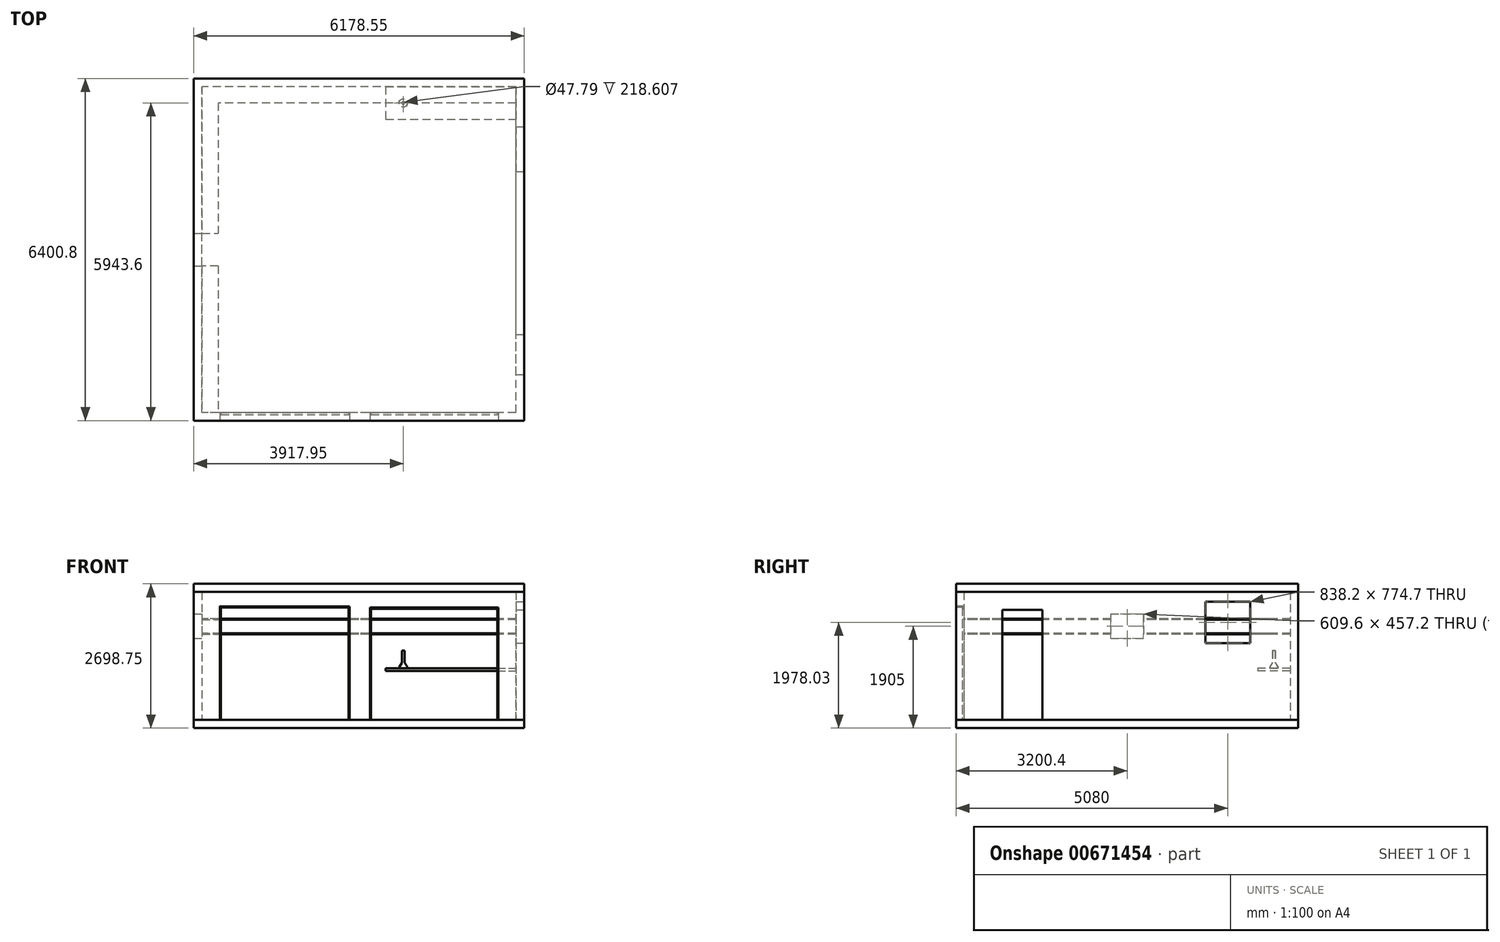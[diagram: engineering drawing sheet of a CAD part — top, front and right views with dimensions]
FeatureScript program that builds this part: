
annotation { "Feature Type Name" : "Feature", "Feature Type Description" : "" }
export const myFeature = defineFeature(function(context is Context, id is Id, definition is map)
    precondition{}
    {
        {
            var Q0;
            Q0=qCreatedBy(makeId("Top.planeOp"),FACE);
            var sketch = newSketch(context, id + "F0", { "sketchPlane" : qUnion([Q0])});
            skLineSegment(sketch, "E0.bottom", {"start": v(0, 0) * mm, "end": v(-5873.75, 0) * mm});
            skLineSegment(sketch, "E0.top", {"start": v(0, 6096) * mm, "end": v(-5873.75, 6096) * mm});
            skLineSegment(sketch, "E0.left", {"start": v(0, 0) * mm, "end": v(0, 6096) * mm});
            skLineSegment(sketch, "E0.right", {"start": v(-5873.75, 0) * mm, "end": v(-5873.75, 6096) * mm});
            skLineSegment(sketch, "E1.0", {"start": v(152.4, 6248.4) * mm, "end": v(-6026.15, 6248.4) * mm});
            skLineSegment(sketch, "E1.1", {"start": v(152.4, -152.4) * mm, "end": v(152.4, 6248.4) * mm});
            skLineSegment(sketch, "E1.2", {"start": v(152.4, -152.4) * mm, "end": v(-6026.15, -152.4) * mm});
            skLineSegment(sketch, "E1.3", {"start": v(-6026.15, -152.4) * mm, "end": v(-6026.15, 6248.4) * mm});
            skSolve(sketch);
        }
        {
            var Q0;
            Q0 = qSketchRegion(id + "F0", true);
            extrude(context, id + "F1", {"entities" : qUnion([Q0]), "depth" : 2393.95 * mm, "offsetDistance" : 25.4 * mm});
        }
        {
            var Q0;
            Q0=makeQuery(id+"F1.opExtrude","SWEPT_FACE",FACE,{"disambiguationData":[OSD([sQuery(id+"F0.wireOp",EDGE,"E1.1")])]});
            var sketch = newSketch(context, id + "F2", { "sketchPlane" : qUnion([Q0])});
            skLineSegment(sketch, "E2.bottom", {"start": v(711.2, 0) * mm, "end": v(1460.5, 0) * mm});
            skLineSegment(sketch, "E2.top", {"start": v(711.2, 2057.4) * mm, "end": v(1460.5, 2057.4) * mm});
            skLineSegment(sketch, "E2.left", {"start": v(711.2, 0) * mm, "end": v(711.2, 2057.4) * mm});
            skLineSegment(sketch, "E2.right", {"start": v(1460.5, 0) * mm, "end": v(1460.5, 2057.4) * mm});
            skSolve(sketch);
        }
        {
            var Q0;
            Q0=makeQuery(id+"F2.imprint","IMPRINT",FACE,{"disambiguationData":[TD([[makeQuery(id+"F2.imprint","IMPRINT",EDGE,{"derivedFrom":sQuery(id+"F2.wireOp",EDGE,"E2.bottom")}),1.0]])]});
            var Q1;
            Q1=makeQuery(id+"F1.opExtrude","SWEPT_FACE",FACE,{"disambiguationData":[OSD([sQuery(id+"F0.wireOp",EDGE,"E0.left")])]});
            extrude(context, id + "F3", {"entities" : qUnion([Q0]), "operationType" : NewBodyOperationType.REMOVE, "endBound" : BoundingType.UP_TO_SURFACE, "oppositeDirection" : true, "depth" : 25.4 * mm, "endBoundEntityFace" : qUnion([Q1]), "offsetDistance" : 25.4 * mm});
        }
        {
            var Q0;
            Q0=makeQuery(id+"F1.opExtrude","SWEPT_FACE",FACE,{"disambiguationData":[OSD([sQuery(id+"F0.wireOp",EDGE,"E1.2")])]});
            var sketch = newSketch(context, id + "F4", { "sketchPlane" : qUnion([Q0])});
            skLineSegment(sketch, "E3.bottom", {"start": v(-5537.2, 0) * mm, "end": v(-3111.5, 0) * mm});
            skLineSegment(sketch, "E3.top", {"start": v(-5537.2, 2125.35) * mm, "end": v(-3111.5, 2120.9) * mm});
            skLineSegment(sketch, "E3.left", {"start": v(-5537.2, 0) * mm, "end": v(-5537.2, 2125.35) * mm});
            skLineSegment(sketch, "E3.right", {"start": v(-3111.5, 0) * mm, "end": v(-3111.5, 2120.9) * mm});
            skLineSegment(sketch, "E4.bottom", {"start": v(-2730.5, 0) * mm, "end": v(-330.2, 0) * mm});
            skLineSegment(sketch, "E4.top", {"start": v(-2730.5, 2101.85) * mm, "end": v(-330.2, 2105.03) * mm});
            skLineSegment(sketch, "E4.left", {"start": v(-2730.5, 0) * mm, "end": v(-2730.5, 2101.85) * mm});
            skLineSegment(sketch, "E4.right", {"start": v(-330.2, 0) * mm, "end": v(-330.2, 2105.03) * mm});
            skSolve(sketch);
        }
        {
            var Q0;
            Q0 = qSketchRegion(id + "F4", true);
            var Q1;
            Q1=makeQuery(id+"F1.opExtrude","SWEPT_FACE",FACE,{"disambiguationData":[OSD([sQuery(id+"F0.wireOp",EDGE,"E0.bottom")])]});
            extrude(context, id + "F5", {"entities" : qUnion([Q0]), "operationType" : NewBodyOperationType.REMOVE, "endBound" : BoundingType.UP_TO_SURFACE, "oppositeDirection" : true, "depth" : 25.4 * mm, "endBoundEntityFace" : qUnion([Q1]), "offsetDistance" : 25.4 * mm});
        }
        {
            var Q0;
            {var subQ0=sQuery(id+"F0.wireOp",EDGE,"E0.left");var subQ1=sQuery(id+"F0.wireOp",EDGE,"E0.top");var subQ2=sQuery(id+"F0.wireOp",EDGE,"E0.right");var subQ3=sQuery(id+"F0.wireOp",EDGE,"E0.bottom");var subQ4=sQuery(id+"F0.wireOp",EDGE,"E1.0");var subQ5=sQuery(id+"F0.wireOp",EDGE,"E1.1");var subQ6=sQuery(id+"F0.wireOp",EDGE,"E1.2");var subQ7=sQuery(id+"F0.wireOp",EDGE,"E1.3");Q0=makeQuery(id+"F5.boolean.opBoolean","SPLIT",FACE,{"disambiguationData":[TD([makeQuery(id+"F1.opExtrude","SWEPT_FACE",FACE,{"disambiguationData":[OSD([subQ1])]})])],"derivedFrom":makeQuery(id+"F1.opExtrude","CAP_FACE",FACE,{"disambiguationData":[OSD([subQ3,subQ1,subQ0,subQ2,subQ4,subQ5,subQ6,subQ7])],"isStart":true})});}
            var sketch = newSketch(context, id + "F6", { "sketchPlane" : qUnion([Q0])});
            skPoint(sketch, "E5.0", {"position": v(152.4, -6248.4) * mm});
            skPoint(sketch, "E6.0", {"position": v(-6026.15, 152.4) * mm});
            skLineSegment(sketch, "E7.bottom", {"start": v(152.4, -6248.4) * mm, "end": v(-6026.15, -6248.4) * mm});
            skLineSegment(sketch, "E7.top", {"start": v(152.4, 152.4) * mm, "end": v(-6026.15, 152.4) * mm});
            skLineSegment(sketch, "E7.left", {"start": v(152.4, -6248.4) * mm, "end": v(152.4, 152.4) * mm});
            skLineSegment(sketch, "E7.right", {"start": v(-6026.15, -6248.4) * mm, "end": v(-6026.15, 152.4) * mm});
            skSolve(sketch);
        }
        {
            var Q0;
            Q0 = qSketchRegion(id + "F6", true);
            extrude(context, id + "F7", {"entities" : qUnion([Q0]), "depth" : 152.4 * mm, "offsetDistance" : 25.4 * mm});
        }
        {
            var Q0;
            Q0=makeQuery(id+"F1.opExtrude","CAP_FACE",FACE,{"disambiguationData":[OSD([sQuery(id+"F0.wireOp",EDGE,"E0.bottom"),sQuery(id+"F0.wireOp",EDGE,"E0.top"),sQuery(id+"F0.wireOp",EDGE,"E0.left"),sQuery(id+"F0.wireOp",EDGE,"E0.right"),sQuery(id+"F0.wireOp",EDGE,"E1.0"),sQuery(id+"F0.wireOp",EDGE,"E1.1"),sQuery(id+"F0.wireOp",EDGE,"E1.2"),sQuery(id+"F0.wireOp",EDGE,"E1.3")])],"isStart":false});
            var sketch = newSketch(context, id + "F8", { "sketchPlane" : qUnion([Q0])});
            skPoint(sketch, "E8.0", {"position": v(-6026.15, 6248.4) * mm});
            skPoint(sketch, "E9.0", {"position": v(152.4, -152.4) * mm});
            skLineSegment(sketch, "E10.bottom", {"start": v(152.4, -152.4) * mm, "end": v(-6026.15, -152.4) * mm});
            skLineSegment(sketch, "E10.top", {"start": v(152.4, 6248.4) * mm, "end": v(-6026.15, 6248.4) * mm});
            skLineSegment(sketch, "E10.left", {"start": v(152.4, -152.4) * mm, "end": v(152.4, 6248.4) * mm});
            skLineSegment(sketch, "E10.right", {"start": v(-6026.15, -152.4) * mm, "end": v(-6026.15, 6248.4) * mm});
            skSolve(sketch);
        }
        {
            var Q0;
            Q0 = qSketchRegion(id + "F8", true);
            extrude(context, id + "F9", {"entities" : qUnion([Q0]), "depth" : 152.4 * mm, "offsetDistance" : 25.4 * mm});
        }
        {
            var Q0;
            Q0=makeQuery(id+"F7.opExtrude","CAP_FACE",FACE,{"disambiguationData":[OSD([sQuery(id+"F6.wireOp",EDGE,"E7.bottom"),sQuery(id+"F6.wireOp",EDGE,"E7.top"),sQuery(id+"F6.wireOp",EDGE,"E7.left"),sQuery(id+"F6.wireOp",EDGE,"E7.right")])],"isStart":true});
            var sketch = newSketch(context, id + "F10", { "sketchPlane" : qUnion([Q0])});
            skLineSegment(sketch, "E11.0", {"start": v(-5537.2, 0) * mm, "end": v(-5873.75, 0) * mm});
            skLineSegment(sketch, "E12.0", {"start": v(-5537.2, 0) * mm, "end": v(-5537.2, -152.4) * mm});
            skLineSegment(sketch, "E13.0", {"start": v(152.4, -152.4) * mm, "end": v(-6026.15, -152.4) * mm});
            skLineSegment(sketch, "E14", {"start": v(-5537.2, -76.2) * mm, "end": v(-5410.2, -76.2) * mm, "construction": true});
            skPoint(sketch, "E14.endSnap0", {"position": v(-5537.2, -76.2) * mm});
            skLineSegment(sketch, "E15", {"start": v(-5575.3, 0) * mm, "end": v(-5575.3, 12.7) * mm});
            skLineSegment(sketch, "E16", {"start": v(-5575.3, 12.7) * mm, "end": v(-5524.5, 12.7) * mm});
            skLineSegment(sketch, "E17", {"start": v(-5524.5, 12.7) * mm, "end": v(-5524.5, -57.15) * mm});
            skLineSegment(sketch, "E18", {"start": v(-5524.5, -57.15) * mm, "end": v(-5511.8, -57.15) * mm});
            skLineSegment(sketch, "E19", {"start": v(-5511.8, -57.15) * mm, "end": v(-5511.8, -76.2) * mm});
            skPoint(sketch, "E19.endSnap0", {"position": v(-5473.7, -76.2) * mm});
            skLineSegment(sketch, "E20.MirrorCS", {"start": v(-5511.8, -95.25) * mm, "end": v(-5511.8, -76.2) * mm});
            skLineSegment(sketch, "E21.MirrorCS", {"start": v(-5524.5, -95.25) * mm, "end": v(-5511.8, -95.25) * mm});
            skLineSegment(sketch, "E22.MirrorCS", {"start": v(-5524.5, -165.1) * mm, "end": v(-5524.5, -95.25) * mm});
            skLineSegment(sketch, "E23.MirrorCS", {"start": v(-5575.3, -165.1) * mm, "end": v(-5524.5, -165.1) * mm});
            skLineSegment(sketch, "E24.MirrorCS", {"start": v(-5575.3, -152.4) * mm, "end": v(-5575.3, -165.1) * mm});
            skSolve(sketch);
        }
        {
            var Q0;
            Q0=makeQuery(id+"F7.opExtrude","CAP_FACE",FACE,{"disambiguationData":[OSD([sQuery(id+"F6.wireOp",EDGE,"E7.bottom"),sQuery(id+"F6.wireOp",EDGE,"E7.top"),sQuery(id+"F6.wireOp",EDGE,"E7.left"),sQuery(id+"F6.wireOp",EDGE,"E7.right")])],"isStart":true});
            var sketch = newSketch(context, id + "F11", { "sketchPlane" : qUnion([Q0])});
            skLineSegment(sketch, "E25.0", {"start": v(152.4, -152.4) * mm, "end": v(152.4, 711.2) * mm});
            skLineSegment(sketch, "E26.0", {"start": v(0, 711.2) * mm, "end": v(152.4, 711.2) * mm});
            skLineSegment(sketch, "E27.0", {"start": v(0, 0) * mm, "end": v(0, 711.2) * mm});
            skLineSegment(sketch, "E28", {"start": v(76.2, 711.2) * mm, "end": v(76.2, 723.9) * mm, "construction": true});
            skPoint(sketch, "E28.endSnap0", {"position": v(76.2, 711.2) * mm});
            skLineSegment(sketch, "E29", {"start": v(76.2, 723.9) * mm, "end": v(-12.7, 723.9) * mm});
            skLineSegment(sketch, "E30", {"start": v(-12.7, 723.9) * mm, "end": v(-12.7, 673.1) * mm});
            skLineSegment(sketch, "E31", {"start": v(-12.7, 673.1) * mm, "end": v(0, 673.1) * mm});
            skLineSegment(sketch, "E32.MirrorCS", {"start": v(76.2, 723.9) * mm, "end": v(165.1, 723.9) * mm});
            skLineSegment(sketch, "E33.MirrorCS", {"start": v(165.1, 723.9) * mm, "end": v(165.1, 673.1) * mm});
            skLineSegment(sketch, "E34.MirrorCS", {"start": v(165.1, 673.1) * mm, "end": v(152.4, 673.1) * mm});
            skSolve(sketch);
        }
        {
            var Q0;
            Q0=makeQuery(id+"F1.opExtrude","SWEPT_FACE",FACE,{"disambiguationData":[OSD([sQuery(id+"F0.wireOp",EDGE,"E0.right")])]});
            var sketch = newSketch(context, id + "F12", { "sketchPlane" : qUnion([Q0])});
            skLineSegment(sketch, "E35.bottom", {"start": v(2743.2, 1981.2) * mm, "end": v(3352.8, 1981.2) * mm});
            skLineSegment(sketch, "E35.top", {"start": v(2743.2, 1524) * mm, "end": v(3352.8, 1524) * mm});
            skLineSegment(sketch, "E35.left", {"start": v(2743.2, 1981.2) * mm, "end": v(2743.2, 1524) * mm});
            skLineSegment(sketch, "E35.right", {"start": v(3352.8, 1981.2) * mm, "end": v(3352.8, 1524) * mm});
            skSolve(sketch);
        }
        {
            var Q0;
            Q0 = qSketchRegion(id + "F12", true);
            var Q1;
            Q1=makeQuery(id+"F1.opExtrude","SWEPT_FACE",FACE,{"disambiguationData":[OSD([sQuery(id+"F0.wireOp",EDGE,"E1.3")])]});
            extrude(context, id + "F13", {"entities" : qUnion([Q0]), "operationType" : NewBodyOperationType.REMOVE, "endBound" : BoundingType.UP_TO_SURFACE, "oppositeDirection" : true, "depth" : 25.4 * mm, "endBoundEntityFace" : qUnion([Q1]), "offsetDistance" : 25.4 * mm});
        }
        {
            var Q0;
            Q0=makeQuery(id+"F13.boolean.opBoolean","COPY",FACE,{"derivedFrom":makeQuery(id+"F13.opExtrude","SWEPT_FACE",FACE,{"disambiguationData":[OSD([sQuery(id+"F12.wireOp",EDGE,"E35.top")])]})});
            var sketch = newSketch(context, id + "F14", { "sketchPlane" : qUnion([Q0])});
            skLineSegment(sketch, "E36.0", {"start": v(-5873.75, 3352.8) * mm, "end": v(-5873.75, 6096) * mm});
            skLineSegment(sketch, "E37.0", {"start": v(0, 6096) * mm, "end": v(-5873.75, 6096) * mm});
            skPoint(sketch, "E38.0", {"position": v(-5873.75, 3352.8) * mm});
            skPoint(sketch, "E39.orphan", {"position": v(-5873.75, 0) * mm});
            skLineSegment(sketch, "E40.0", {"start": v(-5873.75, 0) * mm, "end": v(-5873.75, 2743.2) * mm});
            skPoint(sketch, "E41.0", {"position": v(-5873.75, 2743.2) * mm});
            skSolve(sketch);
        }
        {
            var Q0;
            Q0=makeQuery(id+"F1.opExtrude","SWEPT_FACE",FACE,{"disambiguationData":[OSD([sQuery(id+"F0.wireOp",EDGE,"E0.left")])]});
            var sketch = newSketch(context, id + "F15", { "sketchPlane" : qUnion([Q0])});
            skLineSegment(sketch, "E42.bottom", {"start": v(-6096, 1600.2) * mm, "end": v(-5791.2, 1600.2) * mm});
            skLineSegment(sketch, "E42.top", {"start": v(-6096, 1619.25) * mm, "end": v(-5791.2, 1619.25) * mm});
            skLineSegment(sketch, "E42.left", {"start": v(-6096, 1600.2) * mm, "end": v(-6096, 1619.25) * mm});
            skLineSegment(sketch, "E42.right", {"start": v(-5791.2, 1600.2) * mm, "end": v(-5791.2, 1619.25) * mm});
            skLineSegment(sketch, "E43.bottom", {"start": v(-6096, 1873.25) * mm, "end": v(-5791.2, 1873.25) * mm});
            skLineSegment(sketch, "E43.top", {"start": v(-6096, 1892.3) * mm, "end": v(-5791.2, 1892.3) * mm});
            skLineSegment(sketch, "E43.left", {"start": v(-6096, 1873.25) * mm, "end": v(-6096, 1892.3) * mm});
            skLineSegment(sketch, "E43.right", {"start": v(-5791.2, 1873.25) * mm, "end": v(-5791.2, 1892.3) * mm});
            skSolve(sketch);
        }
        {
            var Q0;
            Q0=makeQuery(id+"F15.imprint","IMPRINT",FACE,{"disambiguationData":[TD([[makeQuery(id+"F15.imprint","IMPRINT",EDGE,{"derivedFrom":sQuery(id+"F15.wireOp",EDGE,"E43.bottom")}),1.0]])]});
            var Q1;
            Q1=makeQuery(id+"F15.imprint","IMPRINT",FACE,{"disambiguationData":[TD([[makeQuery(id+"F15.imprint","IMPRINT",EDGE,{"derivedFrom":sQuery(id+"F15.wireOp",EDGE,"E42.bottom")}),1.0]])]});
            var Q2;
            Q2=sQuery(id+"F14.wireOp",EDGE,"E37.0");
            var Q3;
            Q3=sQuery(id+"F14.wireOp",EDGE,"E36.0");
            sweep(context, id + "F16", {"profiles" : qUnion([Q0, Q1]), "path" : qUnion([Q2, Q3])});
        }
        {
            var Q0;
            Q0=makeQuery(id+"F13.boolean.opBoolean","COPY",FACE,{"derivedFrom":makeQuery(id+"F13.opExtrude","SWEPT_FACE",FACE,{"disambiguationData":[OSD([sQuery(id+"F12.wireOp",EDGE,"E35.left")])]})});
            var sketch = newSketch(context, id + "F17", { "sketchPlane" : qUnion([Q0])});
            skLineSegment(sketch, "E44.0.0", {"start": v(5568.95, 1892.3) * mm, "end": v(5873.75, 1892.3) * mm});
            skLineSegment(sketch, "E44.0.1", {"start": v(5873.75, 1892.3) * mm, "end": v(5873.75, 1873.25) * mm});
            skLineSegment(sketch, "E44.0.2", {"start": v(5873.75, 1873.25) * mm, "end": v(5568.95, 1873.25) * mm});
            skLineSegment(sketch, "E44.0.3", {"start": v(5568.95, 1873.25) * mm, "end": v(5568.95, 1892.3) * mm});
            skLineSegment(sketch, "E45.0.0", {"start": v(5568.95, 1619.25) * mm, "end": v(5873.75, 1619.25) * mm});
            skLineSegment(sketch, "E45.0.1", {"start": v(5873.75, 1619.25) * mm, "end": v(5873.75, 1600.2) * mm});
            skLineSegment(sketch, "E45.0.2", {"start": v(5873.75, 1600.2) * mm, "end": v(5568.95, 1600.2) * mm});
            skLineSegment(sketch, "E45.0.3", {"start": v(5568.95, 1600.2) * mm, "end": v(5568.95, 1619.25) * mm});
            skSolve(sketch);
        }
        {
            var Q0;
            Q0=makeQuery(id+"F17.imprint","IMPRINT",FACE,{"disambiguationData":[TD([[makeQuery(id+"F17.imprint","IMPRINT",EDGE,{"derivedFrom":sQuery(id+"F17.wireOp",EDGE,"E44.0.0")}),-1.0]])]});
            var Q1;
            Q1=makeQuery(id+"F17.imprint","IMPRINT",FACE,{"disambiguationData":[TD([[makeQuery(id+"F17.imprint","IMPRINT",EDGE,{"derivedFrom":sQuery(id+"F17.wireOp",EDGE,"E45.0.0")}),-1.0]])]});
            var Q2;
            Q2=sQuery(id+"F14.wireOp",EDGE,"E40.0");
            sweep(context, id + "F18", {"profiles" : qUnion([Q0, Q1]), "path" : qUnion([Q2])});
        }
        {
            var Q0;
            Q0=makeQuery(id+"F7.opExtrude","CAP_FACE",FACE,{"disambiguationData":[OSD([sQuery(id+"F6.wireOp",EDGE,"E7.bottom"),sQuery(id+"F6.wireOp",EDGE,"E7.top"),sQuery(id+"F6.wireOp",EDGE,"E7.left"),sQuery(id+"F6.wireOp",EDGE,"E7.right")])],"isStart":true});
            cPlane(context, id + "F19", {"entities" : qUnion([Q0]), "cplaneType" : CPlaneType.OFFSET, "offset" : 914.4 * mm, "width" : 152.4 * mm, "height" : 152.4 * mm});
        }
        {
            var Q0;
            Q0=qCreatedBy(id+"F19.planeOp",FACE);
            var sketch = newSketch(context, id + "F20", { "sketchPlane" : qUnion([Q0])});
            skLineSegment(sketch, "E46.0", {"start": v(-5537.2, 0) * mm, "end": v(-5873.75, 0) * mm});
            skLineSegment(sketch, "E47.0", {"start": v(-5873.75, 0) * mm, "end": v(-5873.75, 6096) * mm});
            skLineSegment(sketch, "E48.bottom", {"start": v(-5873.75, 0) * mm, "end": v(-5537.2, 0) * mm});
            skLineSegment(sketch, "E48.top", {"start": v(-5873.75, 2438.4) * mm, "end": v(-5537.2, 2438.4) * mm, "construction": true});
            skLineSegment(sketch, "E48.left", {"start": v(-5873.75, 0) * mm, "end": v(-5873.75, 2438.4) * mm});
            skLineSegment(sketch, "E48.right", {"start": v(-5537.2, 0) * mm, "end": v(-5537.2, 2438.4) * mm});
            skLineSegment(sketch, "E49.bottom", {"start": v(-2438.4, 6096) * mm, "end": v(0, 6096) * mm});
            skLineSegment(sketch, "E49.top", {"start": v(-2438.4, 5486.4) * mm, "end": v(0, 5486.4) * mm});
            skLineSegment(sketch, "E49.left", {"start": v(-2438.4, 6096) * mm, "end": v(-2438.4, 5486.4) * mm});
            skLineSegment(sketch, "E49.right", {"start": v(0, 6096) * mm, "end": v(0, 5486.4) * mm});
            skSolve(sketch);
        }
        {
            var Q0;
            Q0 = qSketchRegion(id + "F20", true);
            extrude(context, id + "F21", {"entities" : qUnion([Q0]), "depth" : 50.8 * mm, "offsetDistance" : 25.4 * mm});
        }
        {
            var Q0;
            Q0=makeQuery(id+"F21.opExtrude","CAP_FACE",FACE,{"disambiguationData":[OSD([sQuery(id+"F20.wireOp",EDGE,"E49.bottom"),sQuery(id+"F20.wireOp",EDGE,"E49.top"),sQuery(id+"F20.wireOp",EDGE,"E49.left"),sQuery(id+"F20.wireOp",EDGE,"E49.right")])],"isStart":false});
            var sketch = newSketch(context, id + "F22", { "sketchPlane" : qUnion([Q0])});
            skCircle(sketch, "E50", {"center": v(-2108.2, 5791.2) * mm, "radius": 88.9 * mm});
            skSolve(sketch);
        }
        {
            var Q0;
            Q0=makeQuery(id+"F22.imprint","IMPRINT",FACE,{"disambiguationData":[TD([[makeQuery(id+"F22.imprint","IMPRINT",EDGE,{"derivedFrom":sQuery(id+"F22.wireOp",EDGE,"E50")}),1.0]])]});
            var Q1;
            Q1=sQuery(id+"F22.wireOp",EDGE,"E50");
            extrude(context, id + "F23", {"entities" : qUnion([Q0]), "surfaceEntities" : qUnion([Q1]), "depth" : 127 * mm, "offsetDistance" : 25.4 * mm, "hasDraft" : true, "draftAngle" : 30 * degree, "draftPullDirection" : true});
        }
        {
            var Q0;
            Q0=makeQuery(id+"F23.opExtrude","CAP_FACE",FACE,{"disambiguationData":[OSD([sQuery(id+"F22.wireOp",EDGE,"E50")])],"isStart":false});
            var sketch = newSketch(context, id + "F24", { "sketchPlane" : qUnion([Q0])});
            skCircle(sketch, "E51", {"center": v(-2108.2, 5791.2) * mm, "radius": 26.44 * mm});
            skSolve(sketch);
        }
        {
            var Q0;
            Q0 = qSketchRegion(id + "F24", true);
            extrude(context, id + "F25", {"entities" : qUnion([Q0]), "operationType" : NewBodyOperationType.ADD, "depth" : 203.2 * mm, "offsetDistance" : 25.4 * mm, "hasSecondDirection" : true, "secondDirectionOppositeDirection" : true, "secondDirectionDepth" : 50.8 * mm});
        }
        {
            var Q0;
            Q0=makeQuery(id+"F25.boolean.opBoolean","INTERSECT",EDGE,{"derivedFrom":[makeQuery(id+"F23.opExtrude","SWEPT_FACE",FACE,{"disambiguationData":[OSD([sQuery(id+"F22.wireOp",EDGE,"E50")])]}),makeQuery(id+"F25.opExtrude","SWEPT_FACE",FACE,{"disambiguationData":[OSD([sQuery(id+"F24.wireOp",EDGE,"E51")])]})]});
            var Q1;
            Q1=makeQuery(id+"F23.opExtrude","CAP_EDGE",EDGE,{"disambiguationData":[OSD([sQuery(id+"F22.wireOp",EDGE,"E50")])],"isStart":true});
            fillet(context, id + "F26", {"entities" : qUnion([Q0, Q1]), "radius" : 12.7 * mm, "tangentPropagation" : true, "allowEdgeOverflow" : false});
        }
        {
            var Q0;
            Q0=makeQuery(id+"F25.opExtrude","CAP_FACE",FACE,{"disambiguationData":[OSD([sQuery(id+"F24.wireOp",EDGE,"E51")])],"isStart":false});
            shell(context, id + "F27", {"entities" : qUnion([Q0]), "thickness" : 2.54 * mm});
        }
        {
            var Q0;
            Q0=makeQuery(id+"F1.opExtrude","SWEPT_FACE",FACE,{"disambiguationData":[OSD([sQuery(id+"F0.wireOp",EDGE,"E1.1")])]});
            var sketch = newSketch(context, id + "F28", { "sketchPlane" : qUnion([Q0])});
            skLineSegment(sketch, "E52.bottom", {"start": v(5346.7, 2212.98) * mm, "end": v(4508.5, 2212.98) * mm});
            skLineSegment(sketch, "E52.top", {"start": v(5346.7, 1438.27) * mm, "end": v(4508.5, 1438.27) * mm});
            skLineSegment(sketch, "E52.left", {"start": v(5346.7, 2212.98) * mm, "end": v(5346.7, 1438.27) * mm});
            skLineSegment(sketch, "E52.right", {"start": v(4508.5, 2212.98) * mm, "end": v(4508.5, 1438.27) * mm});
            skSolve(sketch);
        }
        {
            var Q0;
            Q0 = qSketchRegion(id + "F28", true);
            var Q1;
            Q1=makeQuery(id+"F1.opExtrude","SWEPT_FACE",FACE,{"disambiguationData":[OSD([sQuery(id+"F0.wireOp",EDGE,"E0.left")])]});
            extrude(context, id + "F29", {"entities" : qUnion([Q0]), "operationType" : NewBodyOperationType.REMOVE, "endBound" : BoundingType.UP_TO_SURFACE, "oppositeDirection" : true, "depth" : 25.4 * mm, "endBoundEntityFace" : qUnion([Q1]), "offsetDistance" : 25.4 * mm});
        }
        {
            var Q0;
            Q0=makeQuery(id+"F7.opExtrude","CAP_FACE",FACE,{"disambiguationData":[OSD([sQuery(id+"F6.wireOp",EDGE,"E7.bottom"),sQuery(id+"F6.wireOp",EDGE,"E7.top"),sQuery(id+"F6.wireOp",EDGE,"E7.left"),sQuery(id+"F6.wireOp",EDGE,"E7.right")])],"isStart":true});
            var sketch = newSketch(context, id + "F30", { "sketchPlane" : qUnion([Q0])});
            skLineSegment(sketch, "E53", {"start": v(-5537.2, -152.4) * mm, "end": v(-3111.5, -152.4) * mm, "construction": true});
            skLineSegment(sketch, "E54", {"start": v(-3111.5, -152.4) * mm, "end": v(-2730.5, -152.4) * mm, "construction": true});
            skLineSegment(sketch, "E55", {"start": v(-2730.5, -152.4) * mm, "end": v(-330.2, -152.4) * mm, "construction": true});
            skLineSegment(sketch, "E56", {"start": v(-330.2, -152.4) * mm, "end": v(152.4, -152.4) * mm, "construction": true});
            skLineSegment(sketch, "E57", {"start": v(-4324.35, -152.4) * mm, "end": v(-4324.35, 1056.79) * mm, "construction": true});
            skLineSegment(sketch, "E58", {"start": v(-4324.35, 1056.79) * mm, "end": v(-1530.36, 1056.79) * mm, "construction": true});
            skPoint(sketch, "E58.endSnap0", {"position": v(-1530.36, -152.4) * mm});
            skLineSegment(sketch, "E59", {"start": v(-1530.36, 1056.79) * mm, "end": v(-1530.36, -152.4) * mm, "construction": true});
            skLineSegment(sketch, "E60", {"start": v(-2921, -152.4) * mm, "end": v(-2921, 1056.79) * mm, "construction": true});
            skPoint(sketch, "E60.endSnap0", {"position": v(-2927.35, 1056.79) * mm});
            skPoint(sketch, "E61.0", {"position": v(-5537.2, 0) * mm});
            skLineSegment(sketch, "E62.bottom", {"start": v(-5518.15, -38.1) * mm, "end": v(-5537.2, -38.1) * mm});
            skLineSegment(sketch, "E62.top", {"start": v(-5518.15, 0) * mm, "end": v(-5537.2, 0) * mm});
            skLineSegment(sketch, "E62.left", {"start": v(-5518.15, -38.1) * mm, "end": v(-5518.15, 0) * mm});
            skLineSegment(sketch, "E62.right", {"start": v(-5537.2, -38.1) * mm, "end": v(-5537.2, 0) * mm});
            skLineSegment(sketch, "E63.MirrorCS", {"start": v(-3130.55, -38.1) * mm, "end": v(-3111.5, -38.1) * mm});
            skLineSegment(sketch, "E64.MirrorCS", {"start": v(-3130.55, -38.1) * mm, "end": v(-3130.55, 0) * mm});
            skPoint(sketch, "E65.MirrorP", {"position": v(-3111.5, 0) * mm});
            skLineSegment(sketch, "E66.MirrorCS", {"start": v(-3130.55, 0) * mm, "end": v(-3111.5, 0) * mm});
            skLineSegment(sketch, "E67.MirrorCS", {"start": v(-3111.5, -38.1) * mm, "end": v(-3111.5, 0) * mm});
            skLineSegment(sketch, "E68.MirrorCS", {"start": v(-2711.45, 0) * mm, "end": v(-2730.5, 0) * mm});
            skLineSegment(sketch, "E69.MirrorCS", {"start": v(-2711.45, -38.1) * mm, "end": v(-2730.5, -38.1) * mm});
            skLineSegment(sketch, "E70.MirrorCS", {"start": v(-2711.45, -38.1) * mm, "end": v(-2711.45, 0) * mm});
            skLineSegment(sketch, "E71.MirrorCS", {"start": v(-2730.5, -38.1) * mm, "end": v(-2730.5, 0) * mm});
            skPoint(sketch, "E72.MirrorP", {"position": v(-2730.5, 0) * mm});
            skLineSegment(sketch, "E73.MirrorCS", {"start": v(-330.2, -38.1) * mm, "end": v(-330.2, 0) * mm});
            skPoint(sketch, "E74.MirrorP", {"position": v(-330.2, 0) * mm});
            skLineSegment(sketch, "E75.MirrorCS", {"start": v(-349.26, -38.1) * mm, "end": v(-349.26, 0) * mm});
            skLineSegment(sketch, "E76.MirrorCS", {"start": v(-349.26, -38.1) * mm, "end": v(-330.2, -38.1) * mm});
            skLineSegment(sketch, "E77.MirrorCS", {"start": v(-349.26, 0) * mm, "end": v(-330.2, 0) * mm});
            skSolve(sketch);
        }
        {
            var Q0;
            Q0=makeQuery(id+"F30.imprint","IMPRINT",FACE,{"disambiguationData":[TD([[makeQuery(id+"F30.imprint","IMPRINT",EDGE,{"derivedFrom":sQuery(id+"F30.wireOp",EDGE,"E62.bottom")}),-1.0]])]});
            var Q1;
            Q1=makeQuery(id+"F5.boolean.opBoolean","COPY",FACE,{"derivedFrom":makeQuery(id+"F5.opExtrude","SWEPT_FACE",FACE,{"disambiguationData":[OSD([sQuery(id+"F4.wireOp",EDGE,"E3.top")])]})});
            extrude(context, id + "F31", {"entities" : qUnion([Q0]), "endBound" : BoundingType.UP_TO_SURFACE, "depth" : 25.4 * mm, "endBoundEntityFace" : qUnion([Q1]), "hasOffset" : true, "offsetDistance" : 6.35 * mm});
        }
        {
            var Q0;
            Q0=makeQuery(id+"F30.imprint","IMPRINT",FACE,{"disambiguationData":[TD([[makeQuery(id+"F30.imprint","IMPRINT",EDGE,{"derivedFrom":sQuery(id+"F30.wireOp",EDGE,"E63.MirrorCS")}),1.0]])]});
            var Q1;
            Q1=makeQuery(id+"F5.boolean.opBoolean","COPY",FACE,{"derivedFrom":makeQuery(id+"F5.opExtrude","SWEPT_FACE",FACE,{"disambiguationData":[OSD([sQuery(id+"F4.wireOp",EDGE,"E3.top")])]})});
            extrude(context, id + "F32", {"entities" : qUnion([Q0]), "endBound" : BoundingType.UP_TO_SURFACE, "depth" : 25.4 * mm, "endBoundEntityFace" : qUnion([Q1]), "hasOffset" : true, "offsetDistance" : 6.35 * mm});
        }
        {
            var Q0;
            Q0=makeQuery(id+"F30.imprint","IMPRINT",FACE,{"disambiguationData":[TD([[makeQuery(id+"F30.imprint","IMPRINT",EDGE,{"derivedFrom":sQuery(id+"F30.wireOp",EDGE,"E68.MirrorCS")}),1.0]])]});
            var Q1;
            Q1=makeQuery(id+"F30.imprint","IMPRINT",FACE,{"disambiguationData":[TD([[makeQuery(id+"F30.imprint","IMPRINT",EDGE,{"derivedFrom":sQuery(id+"F30.wireOp",EDGE,"E73.MirrorCS")}),1.0]])]});
            var Q2;
            Q2=makeQuery(id+"F5.boolean.opBoolean","COPY",FACE,{"derivedFrom":makeQuery(id+"F5.opExtrude","SWEPT_FACE",FACE,{"disambiguationData":[OSD([sQuery(id+"F4.wireOp",EDGE,"E4.top")])]})});
            extrude(context, id + "F33", {"entities" : qUnion([Q0, Q1]), "endBound" : BoundingType.UP_TO_SURFACE, "depth" : 25.4 * mm, "endBoundEntityFace" : qUnion([Q2]), "hasOffset" : true, "offsetDistance" : 6.35 * mm});
        }
        {
            var Q0;
            Q0=makeQuery(id+"F31.opExtrude","SWEPT_FACE",FACE,{"disambiguationData":[OSD([sQuery(id+"F30.wireOp",EDGE,"E62.left")])]});
            var sketch = newSketch(context, id + "F34", { "sketchPlane" : qUnion([Q0])});
            skLineSegment(sketch, "E78.bottom", {"start": v(-38.1, 2118.96) * mm, "end": v(0, 2118.96) * mm});
            skLineSegment(sketch, "E78.top", {"start": v(-38.1, 2099.91) * mm, "end": v(0, 2099.91) * mm});
            skLineSegment(sketch, "E78.left", {"start": v(-38.1, 2118.96) * mm, "end": v(-38.1, 2099.91) * mm});
            skLineSegment(sketch, "E78.right", {"start": v(0, 2118.96) * mm, "end": v(0, 2099.91) * mm});
            skSolve(sketch);
        }
        {
            var Q0;
            Q0=makeQuery(id+"F33.opExtrude","SWEPT_FACE",FACE,{"disambiguationData":[OSD([sQuery(id+"F30.wireOp",EDGE,"E69.MirrorCS")])]});
            var sketch = newSketch(context, id + "F35", { "sketchPlane" : qUnion([Q0])});
            skLineSegment(sketch, "E79", {"start": v(-5518.15, 2118.96) * mm, "end": v(-3130.55, 2114.58) * mm});
            skLineSegment(sketch, "E80", {"start": v(-2711.45, 2095.53) * mm, "end": v(-349.26, 2098.65) * mm});
            skSolve(sketch);
        }
        {
            var Q0;
            Q0=makeQuery(id+"F34.imprint","IMPRINT",FACE,{"disambiguationData":[TD([[makeQuery(id+"F34.imprint","IMPRINT",EDGE,{"derivedFrom":sQuery(id+"F34.wireOp",EDGE,"E78.bottom")}),1.0]])]});
            var Q1;
            Q1=sQuery(id+"F35.wireOp",EDGE,"E79");
            sweep(context, id + "F36", {"profiles" : qUnion([Q0]), "path" : qUnion([Q1])});
        }
        {
            var Q0;
            Q0=makeQuery(id+"F33.opExtrude","SWEPT_FACE",FACE,{"disambiguationData":[OSD([sQuery(id+"F30.wireOp",EDGE,"E70.MirrorCS")])]});
            var sketch = newSketch(context, id + "F37", { "sketchPlane" : qUnion([Q0])});
            skLineSegment(sketch, "E81.bottom", {"start": v(-38.1, 2095.53) * mm, "end": v(0, 2095.53) * mm});
            skLineSegment(sketch, "E81.top", {"start": v(-38.1, 2076.48) * mm, "end": v(0, 2076.48) * mm});
            skLineSegment(sketch, "E81.left", {"start": v(-38.1, 2095.53) * mm, "end": v(-38.1, 2076.48) * mm});
            skLineSegment(sketch, "E81.right", {"start": v(0, 2095.53) * mm, "end": v(0, 2076.48) * mm});
            skSolve(sketch);
        }
        {
            var Q0;
            Q0=makeQuery(id+"F37.imprint","IMPRINT",FACE,{"disambiguationData":[TD([[makeQuery(id+"F37.imprint","IMPRINT",EDGE,{"derivedFrom":sQuery(id+"F37.wireOp",EDGE,"E81.bottom")}),1.0]])]});
            var Q1;
            Q1=sQuery(id+"F35.wireOp",EDGE,"E80");
            sweep(context, id + "F38", {"profiles" : qUnion([Q0]), "path" : qUnion([Q1])});
        }
    });
